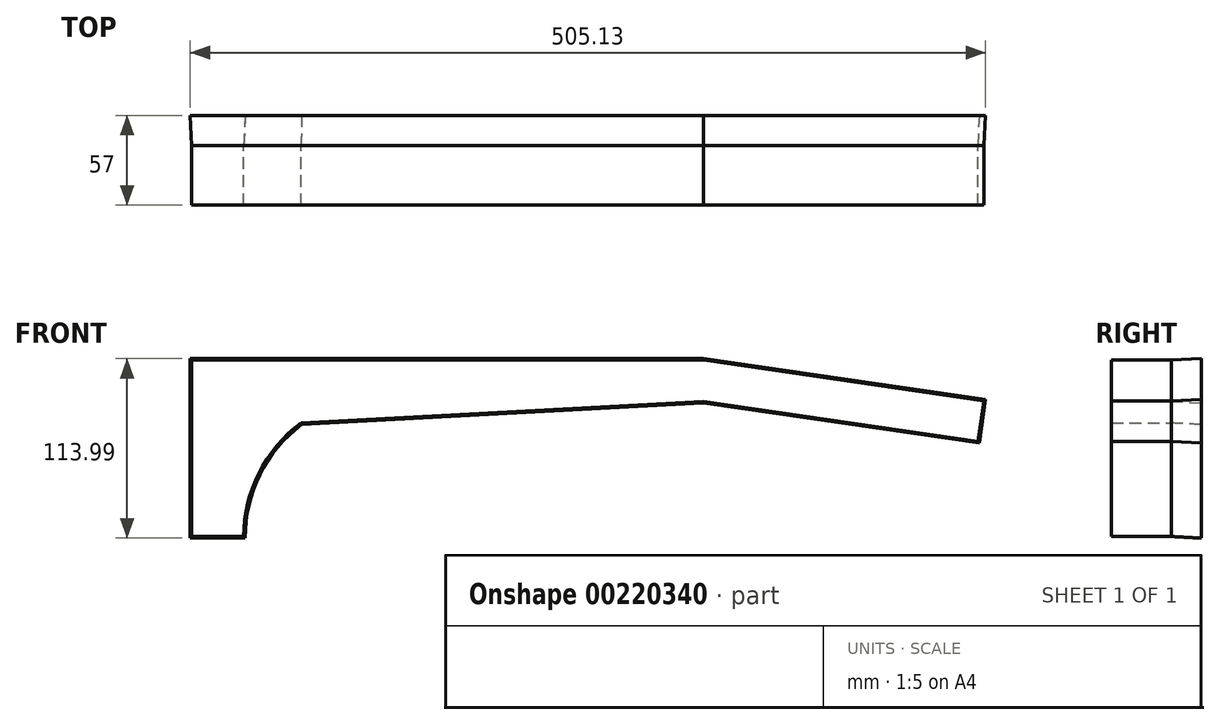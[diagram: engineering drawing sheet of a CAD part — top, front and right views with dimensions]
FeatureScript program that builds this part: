
annotation { "Feature Type Name" : "Feature", "Feature Type Description" : "" }
export const myFeature = defineFeature(function(context is Context, id is Id, definition is map)
    precondition{}
    {
        {
            var Q0;
            Q0=qCreatedBy(makeId("Front.planeOp"),FACE);
            var sketch = newSketch(context, id + "F0", { "sketchPlane" : qUnion([Q0])});
            skLineSegment(sketch, "E0", {"start": v(-104.76, 36.79) * mm, "end": v(-104.76, -75.21) * mm});
            skLineSegment(sketch, "E1", {"start": v(-104.76, -75.21) * mm, "end": v(-71.76, -75.21) * mm});
            skLineSegment(sketch, "E2", {"start": v(220.24, 36.79) * mm, "end": v(398.24, 10.93) * mm});
            skLineSegment(sketch, "E3", {"start": v(-104.76, 36.79) * mm, "end": v(220.24, 36.79) * mm});
            skLineSegment(sketch, "E4", {"start": v(398.24, 10.93) * mm, "end": v(394.5, -14.8) * mm});
            skLineSegment(sketch, "E5", {"start": v(394.5, -14.8) * mm, "end": v(220.24, 10.51) * mm});
            skArc(sketch, "E6", {"start": v(-35.3, -3.13) * mm, "mid": v(-62.13, -34.83) * mm, "end": v(-71.76, -75.21) * mm});
            skLineSegment(sketch, "E7", {"start": v(-35.3, -3.13) * mm, "end": v(220.24, 10.51) * mm});
            skLineSegment(sketch, "E8", {"start": v(-104.76, 36.79) * mm, "end": v(398.24, 36.79) * mm});
            skSolve(sketch);
        }
        {
            var Q0;
            Q0=makeQuery(id+"F0.imprint","IMPRINT",FACE,{"disambiguationData":[TD([[makeQuery(id+"F0.imprint","IMPRINT",EDGE,{"derivedFrom":sQuery(id+"F0.wireOp",EDGE,"E0")}),1.0]])]});
            extrude(context, id + "F1", {"entities" : qUnion([Q0]), "depth" : 19 * mm});
        }
        {
            var Q0;
            Q0=makeQuery(id+"F0.imprint","IMPRINT",FACE,{"disambiguationData":[TD([[makeQuery(id+"F0.imprint","IMPRINT",EDGE,{"derivedFrom":sQuery(id+"F0.wireOp",EDGE,"E0")}),1.0]])]});
            extrude(context, id + "F2", {"entities" : qUnion([Q0]), "operationType" : NewBodyOperationType.ADD, "oppositeDirection" : true, "depth" : 19 * mm, "hasDraft" : true, "draftAngle" : 3 * degree});
        }
        {
            var Q0;
            Q0=makeQuery(id+"F1.opExtrude","CAP_FACE",FACE,{"disambiguationData":[OSD([sQuery(id+"F0.wireOp",EDGE,"E0"),sQuery(id+"F0.wireOp",EDGE,"E1"),sQuery(id+"F0.wireOp",EDGE,"E2"),sQuery(id+"F0.wireOp",EDGE,"E3"),sQuery(id+"F0.wireOp",EDGE,"E4"),sQuery(id+"F0.wireOp",EDGE,"E5"),sQuery(id+"F0.wireOp",EDGE,"E6"),sQuery(id+"F0.wireOp",EDGE,"E7")])],"isStart":false});
            extrude(context, id + "F3", {"entities" : qUnion([Q0]), "operationType" : NewBodyOperationType.ADD, "depth" : 19 * mm});
        }
    });
